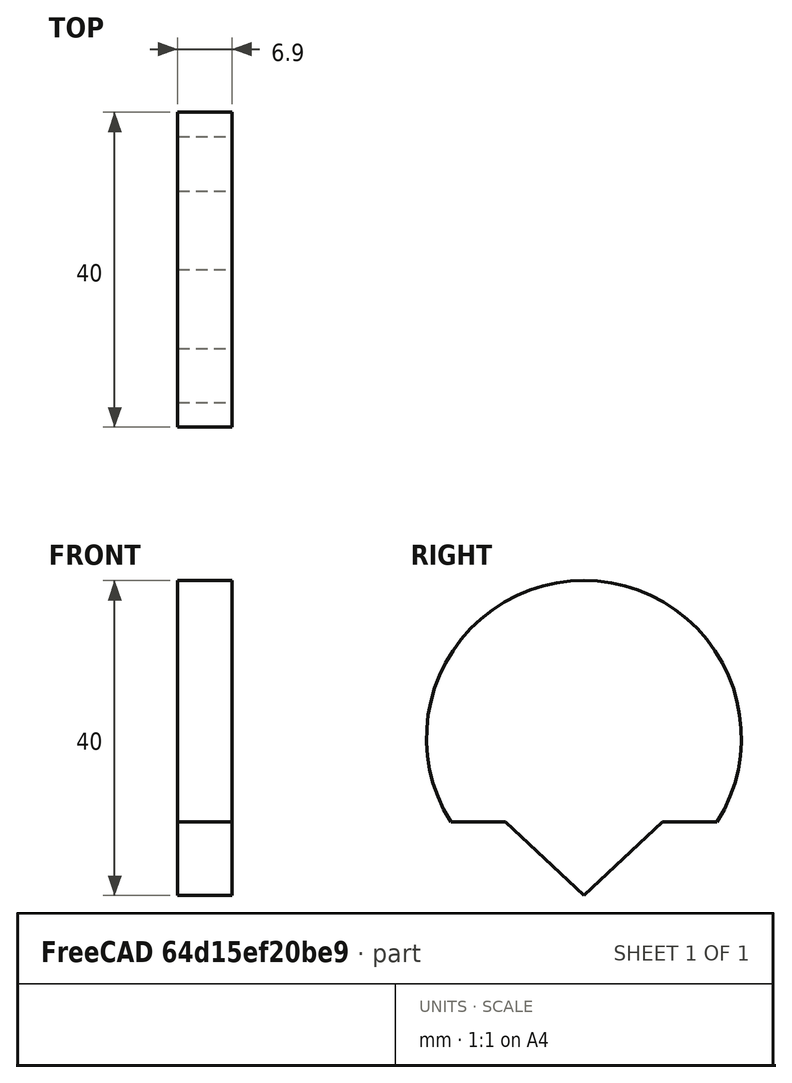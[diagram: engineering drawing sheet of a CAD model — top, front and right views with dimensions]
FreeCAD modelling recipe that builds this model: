
FCSTD DOCUMENT  (FreeCAD 0.19R)
Label: PlotterA
License: All rights reserved
LicenseURL: http://en.wikipedia.org/wiki/All_rights_reserved
objects: App::DocumentObjectGroup×3, PartDesign::CoordinateSystem×2, App::FeaturePython×1, Sketcher::SketchObject×1, PartDesign::Pad×1, PartDesign::Body×1, App::Part×1
note: 6 computed .brp shape members not serialized (recipe doc carries the construction recipe); baked Part::Feature solids carry a one-line shape summary decoded from their .brp

FEATURE [App::DocumentObjectGroup] Parts
FEATURE [PartDesign::CoordinateSystem] LCS_Origin
  AttacherType = Attacher::AttachEngine3D
  MapMode = 2
  Support = -> [X_Axis]
FEATURE [App::DocumentObjectGroup] Constraints
FEATURE [App::FeaturePython] Variables  # WARN: FeaturePython — macro-defined, semantics opaque (R4)
  Type = App::PropertyContainer
FEATURE [App::DocumentObjectGroup] Configurations
FEATURE [Sketcher::SketchObject] Sketch018  label="A_Sketch"
  FullyConstrained = true
  Placement = pos=(37.9,0,0) rot=(0.57735,0.57735,0.57735;2.0944rad)
  sketch-geometry (7):
    g0: ArcOfCircle CenterX=200.05 CenterY=30.7 CenterZ=0 NormalX=0 NormalY=0 NormalZ=1 AngleXU=0 Radius=20 StartAngle=5.71927 EndAngle=9.98869
    g1: LineSegment StartX=200.05 StartY=58.635 StartZ=0 EndX=200.05 EndY=2.765 EndZ=0
    g2: LineSegment StartX=183.147 StartY=20.01 StartZ=0 EndX=190.05 EndY=20.01 EndZ=0
    g3: LineSegment StartX=216.953 StartY=20.01 StartZ=0 EndX=210.05 EndY=20.01 EndZ=0
    g4: LineSegment StartX=190.05 StartY=20.01 StartZ=0 EndX=200.05 EndY=10.7 EndZ=0
    g5: LineSegment StartX=210.05 StartY=20.01 StartZ=0 EndX=200.05 EndY=10.7 EndZ=0
    g6: LineSegment StartX=161.84 StartY=30.7 StartZ=0 EndX=238.26 EndY=30.7 EndZ=0
  constraints (20):
    c: Radius(g0) = 20
    c: Distance(g0,g-1) = 30.7
    c: Symmetric(g0,g0,g1)
    c: Coincident(g2,g0)
    c: Coincident(g3,g0)
    c: Coincident(g4,g2)
    c: PointOnObject(g4,g1)
    c: Coincident(g5,g3)
    c: Coincident(g5,g4)
    c: Symmetric(g2,g3,g1)
    c: Distance(g2,g3) = 20
    c: Angle(g6,g-1) = 0
    c: Distance(g6) = 76.42
    c: Symmetric(g6,g6,g0)
    c: DistanceX(g-2,g0) = 200.05
    c: Parallel(g2,g6)
    c: Distance(g0,g6) = 10.69
    c: Distance(g4,g0) = 20
    c: Symmetric(g1,g1,g6)
    c: Distance(g1) = 55.87
FEATURE [PartDesign::Pad] Pad008
  Direction = (1,1,1)
  Length = 6.9
  Length2 = 100
  Placement = pos=(37.9,0,0) rot=(0.57735,0.57735,0.57735;2.0944rad)
  Profile = -> Sketch018
  Refine = true
  Type = 0
FEATURE [PartDesign::Body] Body008  label="A_Axis"
  Group = -> [Sketch018,Pad008]
  Origin = -> Origin008
  Tip = -> Pad008
FEATURE [PartDesign::CoordinateSystem] LCS_1
  AttacherType = Attacher::AttachEngine3D
  AttachmentOffset = pos=(200.05,30.7,0) rot=(0,0,1;0.506145rad)
  MapMode = 2
  Placement = pos=(37.9,200.05,30.7) rot=(0.652748,0.384498,0.652748;2.40745rad)
  Support = -> [Sketch018]
FEATURE [App::Part] Model
  AssemblyType = Part::Link
  Group = -> [LCS_Origin,Constraints,Variables,Configurations,Body008,LCS_1]
  Origin = -> Origin
  Type = Assembly
